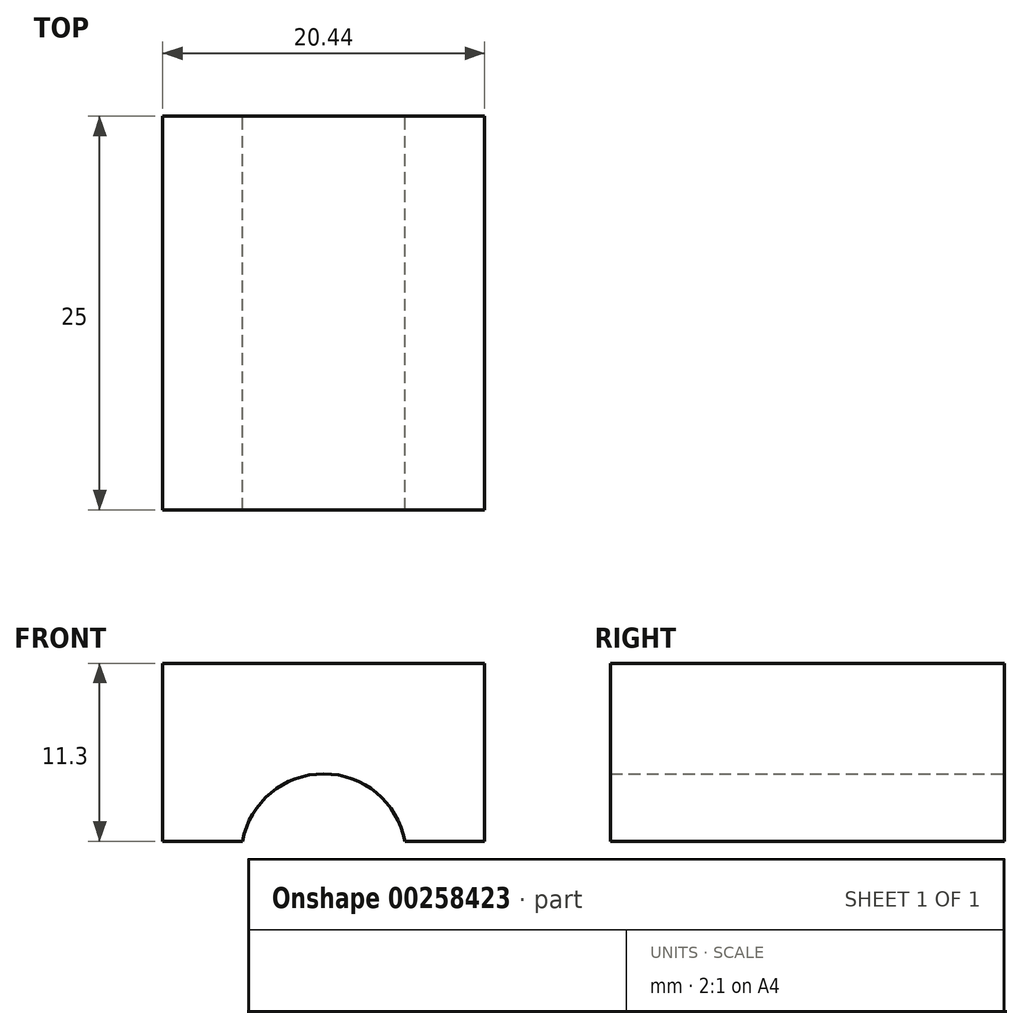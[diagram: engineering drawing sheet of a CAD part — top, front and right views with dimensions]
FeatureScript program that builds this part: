
annotation { "Feature Type Name" : "Feature", "Feature Type Description" : "" }
export const myFeature = defineFeature(function(context is Context, id is Id, definition is map)
    precondition{}
    {
        {
            var Q0;
            Q0=qCreatedBy(makeId("Front.planeOp"),FACE);
            var sketch = newSketch(context, id + "F0", { "sketchPlane" : qUnion([Q0])});
            skArc(sketch, "E0", {"start": v(5.16, 0.06) * mm, "mid": v(0, 4.34) * mm, "end": v(-5.16, 0.06) * mm});
            skLineSegment(sketch, "E1", {"start": v(10.22, 0.06) * mm, "end": v(5.16, 0.06) * mm});
            skLineSegment(sketch, "E2.trimOffspring", {"start": v(-5.16, 0.06) * mm, "end": v(-10.22, 0.06) * mm});
            skLineSegment(sketch, "E3", {"start": v(-10.22, 0.06) * mm, "end": v(-10.22, 11.36) * mm});
            skLineSegment(sketch, "E4", {"start": v(-10.22, 11.36) * mm, "end": v(10.22, 11.36) * mm});
            skLineSegment(sketch, "E5", {"start": v(10.22, 11.36) * mm, "end": v(10.22, 0.06) * mm});
            skLineSegment(sketch, "E6", {"start": v(0, 28.32) * mm, "end": v(0, -17.05) * mm, "construction": true});
            skLineSegment(sketch, "E7", {"start": v(0, 4.34) * mm, "end": v(0, 11.36) * mm, "construction": true});
            skSolve(sketch);
        }
        {
            var Q0;
            Q0 = qSketchRegion(id + "F0", true);
            extrude(context, id + "F1", {"entities" : qUnion([Q0]), "depth" : 25 * mm});
        }
    });
